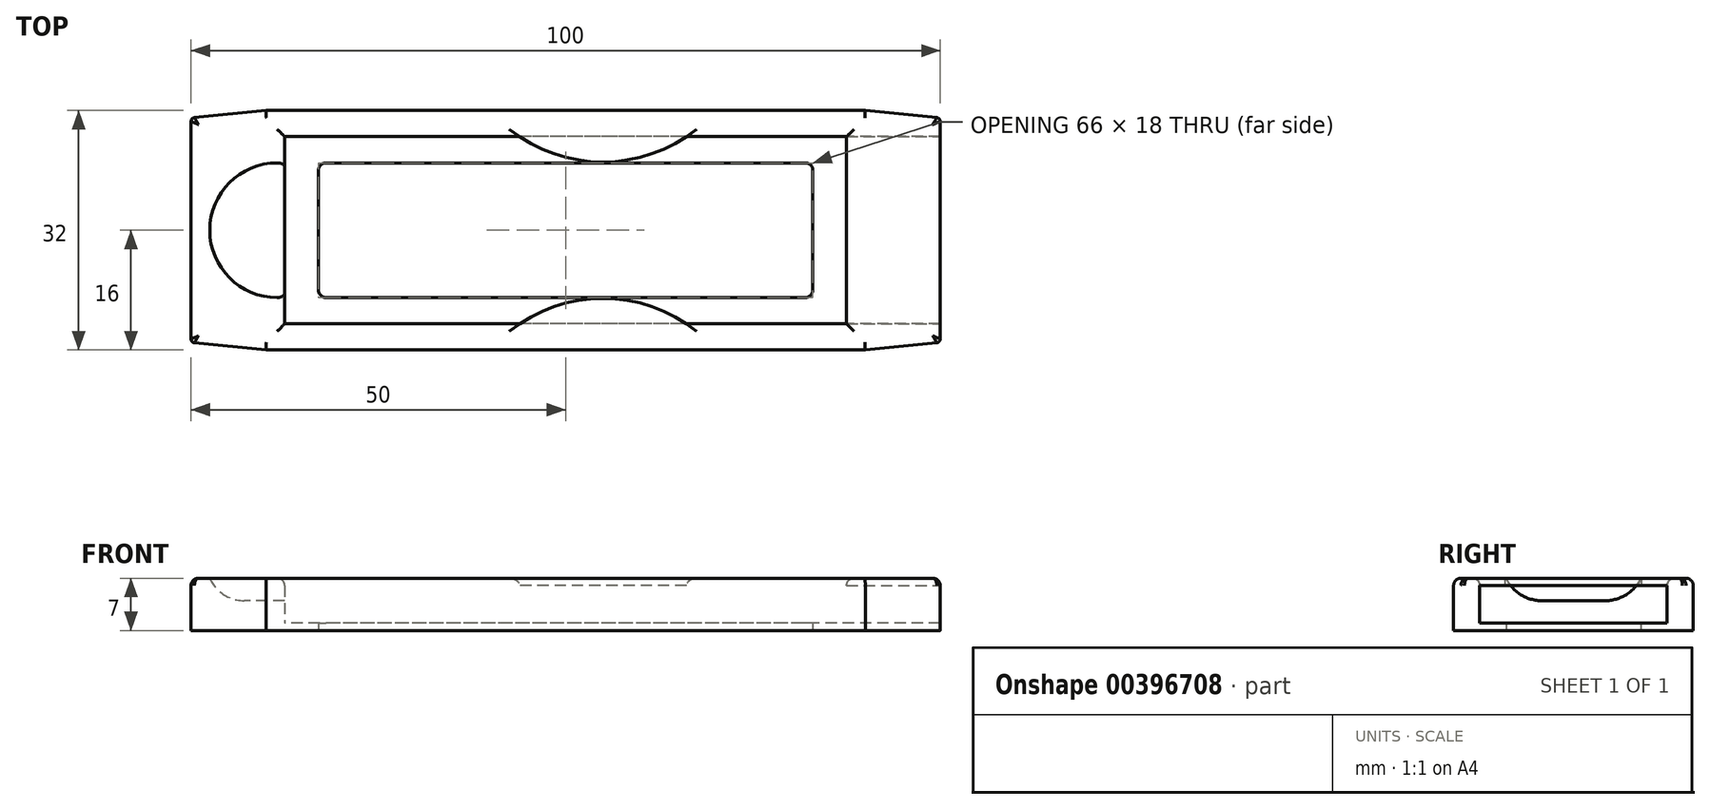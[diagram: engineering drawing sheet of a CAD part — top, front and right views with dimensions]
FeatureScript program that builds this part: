
annotation { "Feature Type Name" : "Feature", "Feature Type Description" : "" }
export const myFeature = defineFeature(function(context is Context, id is Id, definition is map)
    precondition{}
    {
        {
            var Q0;
            Q0=qCreatedBy(makeId("Top.planeOp"),FACE);
            var sketch = newSketch(context, id + "F0", { "sketchPlane" : qUnion([Q0])});
            skLineSegment(sketch, "E0.bottom", {"start": v(37.5, 12.5) * mm, "end": v(-37.5, 12.5) * mm});
            skLineSegment(sketch, "E0.top", {"start": v(37.5, -12.5) * mm, "end": v(-37.5, -12.5) * mm});
            skLineSegment(sketch, "E0.left", {"start": v(37.5, 12.5) * mm, "end": v(37.5, -12.5) * mm});
            skLineSegment(sketch, "E0.right", {"start": v(-37.5, 12.5) * mm, "end": v(-37.5, -12.5) * mm});
            skPoint(sketch, "E0.middle", {"position": v(0, 0) * mm});
            skLineSegment(sketch, "E1.bottom", {"start": v(50, 16) * mm, "end": v(-50, 16) * mm});
            skLineSegment(sketch, "E1.top", {"start": v(50, -16) * mm, "end": v(-50, -16) * mm});
            skLineSegment(sketch, "E1.left", {"start": v(50, 16) * mm, "end": v(50, -16) * mm});
            skLineSegment(sketch, "E1.right", {"start": v(-50, 16) * mm, "end": v(-50, -16) * mm});
            skSolve(sketch);
        }
        {
            var Q0;
            Q0=makeQuery(id+"F0.imprint","IMPRINT",FACE,{"disambiguationData":[TD([[makeQuery(id+"F0.imprint","IMPRINT",EDGE,{"derivedFrom":sQuery(id+"F0.wireOp",EDGE,"E0.bottom")}),-1.0]])]});
            extrude(context, id + "F1", {"entities" : qUnion([Q0]), "depth" : 7 * mm});
        }
        {
            var Q0;
            Q0=makeQuery(id+"F1.opExtrude","SWEPT_EDGE",EDGE,{"disambiguationData":[OSD([sQuery(id+"F0.wireOp",EDGE,"E1.top"),sQuery(id+"F0.wireOp",EDGE,"E1.right")])]});
            var Q1;
            Q1=makeQuery(id+"F1.opExtrude","SWEPT_EDGE",EDGE,{"disambiguationData":[OSD([sQuery(id+"F0.wireOp",EDGE,"E1.top"),sQuery(id+"F0.wireOp",EDGE,"E1.left")])]});
            var Q2;
            Q2=makeQuery(id+"F1.opExtrude","SWEPT_EDGE",EDGE,{"disambiguationData":[OSD([sQuery(id+"F0.wireOp",EDGE,"E1.bottom"),sQuery(id+"F0.wireOp",EDGE,"E1.left")])]});
            var Q3;
            Q3=makeQuery(id+"F1.opExtrude","SWEPT_EDGE",EDGE,{"disambiguationData":[OSD([sQuery(id+"F0.wireOp",EDGE,"E1.bottom"),sQuery(id+"F0.wireOp",EDGE,"E1.right")])]});
            chamfer(context, id + "F2", {"entities" : qUnion([Q0, Q1, Q2, Q3]), "chamferType" : ChamferType.TWO_OFFSETS, "width1" : 10 * mm, "oppositeDirection" : false, "width2" : 1 * mm, "tangentPropagation" : true});
        }
        {
            var Q0;
            {var subQ0=sQuery(id+"F0.wireOp",EDGE,"E1.right");Q0=makeQuery(id+"F2.opChamfer","BLEND_EDGE",EDGE,{"blendedFrom":[makeQuery(id+"F1.opExtrude","SWEPT_EDGE",EDGE,{"disambiguationData":[OSD([sQuery(id+"F0.wireOp",EDGE,"E1.top"),subQ0])]}),makeQuery(id+"F1.opExtrude","SWEPT_FACE",FACE,{"disambiguationData":[OSD([subQ0])]})],"blendedInto":[makeQuery(id+"F1.opExtrude","SWEPT_FACE",FACE,{"disambiguationData":[OSD([subQ0])]})]});}
            var Q1;
            {var subQ0=sQuery(id+"F0.wireOp",EDGE,"E1.left");Q1=makeQuery(id+"F2.opChamfer","BLEND_EDGE",EDGE,{"blendedFrom":[makeQuery(id+"F1.opExtrude","SWEPT_EDGE",EDGE,{"disambiguationData":[OSD([sQuery(id+"F0.wireOp",EDGE,"E1.top"),subQ0])]}),makeQuery(id+"F1.opExtrude","SWEPT_FACE",FACE,{"disambiguationData":[OSD([subQ0])]})],"blendedInto":[makeQuery(id+"F1.opExtrude","SWEPT_FACE",FACE,{"disambiguationData":[OSD([subQ0])]})]});}
            var Q2;
            {var subQ0=sQuery(id+"F0.wireOp",EDGE,"E1.left");Q2=makeQuery(id+"F2.opChamfer","BLEND_EDGE",EDGE,{"blendedFrom":[makeQuery(id+"F1.opExtrude","SWEPT_EDGE",EDGE,{"disambiguationData":[OSD([sQuery(id+"F0.wireOp",EDGE,"E1.bottom"),subQ0])]}),makeQuery(id+"F1.opExtrude","SWEPT_FACE",FACE,{"disambiguationData":[OSD([subQ0])]})],"blendedInto":[makeQuery(id+"F1.opExtrude","SWEPT_FACE",FACE,{"disambiguationData":[OSD([subQ0])]})]});}
            var Q3;
            {var subQ0=sQuery(id+"F0.wireOp",EDGE,"E1.right");Q3=makeQuery(id+"F2.opChamfer","BLEND_EDGE",EDGE,{"blendedFrom":[makeQuery(id+"F1.opExtrude","SWEPT_EDGE",EDGE,{"disambiguationData":[OSD([sQuery(id+"F0.wireOp",EDGE,"E1.bottom"),subQ0])]}),makeQuery(id+"F1.opExtrude","SWEPT_FACE",FACE,{"disambiguationData":[OSD([subQ0])]})],"blendedInto":[makeQuery(id+"F1.opExtrude","SWEPT_FACE",FACE,{"disambiguationData":[OSD([subQ0])]})]});}
            fillet(context, id + "F3", {"entities" : qUnion([Q0, Q1, Q2, Q3]), "radius" : .5 * mm, "tangentPropagation" : true, "allowEdgeOverflow" : false});
        }
        {
            var Q0;
            Q0=qCreatedBy(makeId("Top.planeOp"),FACE);
            var sketch = newSketch(context, id + "F4", { "sketchPlane" : qUnion([Q0])});
            skLineSegment(sketch, "E2.bottom", {"start": v(38, 13) * mm, "end": v(-38, 13) * mm});
            skLineSegment(sketch, "E2.top", {"start": v(38, -13) * mm, "end": v(-38, -13) * mm});
            skLineSegment(sketch, "E2.left", {"start": v(38, 13) * mm, "end": v(38, -13) * mm});
            skLineSegment(sketch, "E2.right", {"start": v(-38, 13) * mm, "end": v(-38, -13) * mm});
            skPoint(sketch, "E2.middle", {"position": v(0, 0) * mm});
            skLineSegment(sketch, "E3.bottom", {"start": v(33, 9) * mm, "end": v(-33, 9) * mm});
            skLineSegment(sketch, "E3.top", {"start": v(33, -9) * mm, "end": v(-33, -9) * mm});
            skLineSegment(sketch, "E3.left", {"start": v(33, 9) * mm, "end": v(33, -9) * mm});
            skLineSegment(sketch, "E3.right", {"start": v(-33, 9) * mm, "end": v(-33, -9) * mm});
            skSolve(sketch);
        }
        {
            var Q0;
            Q0 = qSketchRegion(id + "F4", true);
            extrude(context, id + "F5", {"entities" : qUnion([Q0]), "operationType" : NewBodyOperationType.ADD, "depth" : 1 * mm});
        }
        {
            var Q0;
            Q0=makeQuery(id+"F5.opExtrude","SWEPT_EDGE",EDGE,{"disambiguationData":[OSD([sQuery(id+"F4.wireOp",EDGE,"E3.bottom"),sQuery(id+"F4.wireOp",EDGE,"E3.right")])]});
            var Q1;
            Q1=makeQuery(id+"F5.opExtrude","SWEPT_EDGE",EDGE,{"disambiguationData":[OSD([sQuery(id+"F4.wireOp",EDGE,"E3.bottom"),sQuery(id+"F4.wireOp",EDGE,"E3.left")])]});
            var Q2;
            Q2=makeQuery(id+"F5.opExtrude","SWEPT_EDGE",EDGE,{"disambiguationData":[OSD([sQuery(id+"F4.wireOp",EDGE,"E3.top"),sQuery(id+"F4.wireOp",EDGE,"E3.left")])]});
            var Q3;
            Q3=makeQuery(id+"F5.opExtrude","SWEPT_EDGE",EDGE,{"disambiguationData":[OSD([sQuery(id+"F4.wireOp",EDGE,"E3.top"),sQuery(id+"F4.wireOp",EDGE,"E3.right")])]});
            fillet(context, id + "F6", {"entities" : qUnion([Q0, Q1, Q2, Q3]), "radius" : 1 * mm, "tangentPropagation" : true, "allowEdgeOverflow" : false});
        }
        {
            var Q0;
            Q0=makeQuery(id+"F1.opExtrude","CAP_EDGE",EDGE,{"disambiguationData":[OSD([sQuery(id+"F0.wireOp",EDGE,"E1.bottom")])],"isStart":false});
            var Q1;
            Q1=makeQuery(id+"F1.opExtrude","CAP_EDGE",EDGE,{"disambiguationData":[OSD([sQuery(id+"F0.wireOp",EDGE,"E1.top")])],"isStart":false});
            var Q2;
            Q2=makeQuery(id+"F1.opExtrude","CAP_EDGE",EDGE,{"disambiguationData":[OSD([sQuery(id+"F0.wireOp",EDGE,"E1.right")])],"isStart":false});
            var Q3;
            Q3=makeQuery(id+"F1.opExtrude","CAP_EDGE",EDGE,{"disambiguationData":[OSD([sQuery(id+"F0.wireOp",EDGE,"E1.left")])],"isStart":false});
            var Q4;
            Q4=makeQuery(id+"F1.opExtrude","CAP_EDGE",EDGE,{"disambiguationData":[OSD([sQuery(id+"F0.wireOp",EDGE,"E0.left")])],"isStart":false});
            var Q5;
            Q5=makeQuery(id+"F1.opExtrude","CAP_EDGE",EDGE,{"disambiguationData":[OSD([sQuery(id+"F0.wireOp",EDGE,"E0.top")])],"isStart":false});
            var Q6;
            Q6=makeQuery(id+"F1.opExtrude","CAP_EDGE",EDGE,{"disambiguationData":[OSD([sQuery(id+"F0.wireOp",EDGE,"E0.right")])],"isStart":false});
            var Q7;
            Q7=makeQuery(id+"F1.opExtrude","CAP_EDGE",EDGE,{"disambiguationData":[OSD([sQuery(id+"F0.wireOp",EDGE,"E0.bottom")])],"isStart":false});
            fillet(context, id + "F7", {"entities" : qUnion([Q0, Q1, Q2, Q3, Q4, Q5, Q6, Q7]), "radius" : 1 * mm, "tangentPropagation" : true, "allowEdgeOverflow" : false});
        }
        {
            var Q0;
            Q0=makeQuery(id+"F1.opExtrude","SWEPT_FACE",FACE,{"disambiguationData":[OSD([sQuery(id+"F0.wireOp",EDGE,"E1.left")])]});
            var sketch = newSketch(context, id + "F8", { "sketchPlane" : qUnion([Q0])});
            skLineSegment(sketch, "E4.bottom", {"start": v(12.5, 6) * mm, "end": v(-12.5, 6) * mm});
            skLineSegment(sketch, "E4.top", {"start": v(12.5, 1) * mm, "end": v(-12.5, 1) * mm});
            skLineSegment(sketch, "E4.left", {"start": v(12.5, 6) * mm, "end": v(12.5, 1) * mm});
            skLineSegment(sketch, "E4.right", {"start": v(-12.5, 6) * mm, "end": v(-12.5, 1) * mm});
            skPoint(sketch, "E4.middle", {"position": v(0, 3.5) * mm});
            skPoint(sketch, "E4.middle.positionSnap0", {"position": v(0, 0) * mm});
            skPoint(sketch, "E4.centerSnap0", {"position": v(0, 0) * mm});
            skSolve(sketch);
        }
        {
            var Q0;
            Q0=makeQuery(id+"F8.imprint","IMPRINT",FACE,{"disambiguationData":[TD([[makeQuery(id+"F8.imprint","IMPRINT",EDGE,{"derivedFrom":sQuery(id+"F8.wireOp",EDGE,"E4.bottom")}),1.0]])]});
            extrude(context, id + "F9", {"entities" : qUnion([Q0]), "operationType" : NewBodyOperationType.REMOVE, "oppositeDirection" : true, "depth" : 15 * mm});
        }
        {
            var Q0;
            Q0=makeQuery(id+"F1.opExtrude","CAP_FACE",FACE,{"disambiguationData":[OSD([sQuery(id+"F0.wireOp",EDGE,"E0.bottom"),sQuery(id+"F0.wireOp",EDGE,"E0.top"),sQuery(id+"F0.wireOp",EDGE,"E0.left"),sQuery(id+"F0.wireOp",EDGE,"E0.right"),sQuery(id+"F0.wireOp",EDGE,"E1.bottom"),sQuery(id+"F0.wireOp",EDGE,"E1.top"),sQuery(id+"F0.wireOp",EDGE,"E1.left"),sQuery(id+"F0.wireOp",EDGE,"E1.right")])],"isStart":false});
            var sketch = newSketch(context, id + "F10", { "sketchPlane" : qUnion([Q0])});
            skCircle(sketch, "E5", {"center": v(-38.5, 0) * mm, "radius": 9 * mm});
            skSolve(sketch);
        }
        {
            var Q0;
            Q0 = qSketchRegion(id + "F10", true);
            extrude(context, id + "F11", {"entities" : qUnion([Q0]), "operationType" : NewBodyOperationType.REMOVE, "oppositeDirection" : true, "depth" : 3 * mm});
        }
        {
            var Q0;
            Q0=makeQuery(id+"F11.boolean.opBoolean","COPY",EDGE,{"derivedFrom":makeQuery(id+"F11.opExtrude","CAP_EDGE",EDGE,{"disambiguationData":[OSD([sQuery(id+"F10.wireOp",EDGE,"E5")])],"isStart":false})});
            fillet(context, id + "F12", {"entities" : qUnion([Q0]), "radius" : 5 * mm, "tangentPropagation" : true, "allowEdgeOverflow" : false});
        }
        {
            var Q0;
            Q0=makeQuery(id+"F1.opExtrude","CAP_FACE",FACE,{"disambiguationData":[OSD([sQuery(id+"F0.wireOp",EDGE,"E0.bottom"),sQuery(id+"F0.wireOp",EDGE,"E0.top"),sQuery(id+"F0.wireOp",EDGE,"E0.left"),sQuery(id+"F0.wireOp",EDGE,"E0.right"),sQuery(id+"F0.wireOp",EDGE,"E1.bottom"),sQuery(id+"F0.wireOp",EDGE,"E1.top"),sQuery(id+"F0.wireOp",EDGE,"E1.left"),sQuery(id+"F0.wireOp",EDGE,"E1.right")])],"isStart":false});
            var sketch = newSketch(context, id + "F13", { "sketchPlane" : qUnion([Q0])});
            skArc(sketch, "E6", {"start": v(17.5, -13.5) * mm, "mid": v(5, -9.11) * mm, "end": v(-7.5, -13.5) * mm});
            skLineSegment(sketch, "E7", {"start": v(17.5, -13.5) * mm, "end": v(-7.5, -13.5) * mm});
            skSolve(sketch);
        }
        {
            var Q0;
            Q0 = qSketchRegion(id + "F13", true);
            extrude(context, id + "F14", {"entities" : qUnion([Q0]), "operationType" : NewBodyOperationType.ADD, "oppositeDirection" : true, "depth" : 1 * mm});
        }
        {
            var Q0;
            Q0=makeQuery(id+"F14.boolean.opBoolean","MERGE",FACE,{"derivedFrom":[makeQuery(id+"F1.opExtrude","CAP_FACE",FACE,{"disambiguationData":[OSD([sQuery(id+"F0.wireOp",EDGE,"E0.bottom"),sQuery(id+"F0.wireOp",EDGE,"E0.top"),sQuery(id+"F0.wireOp",EDGE,"E0.left"),sQuery(id+"F0.wireOp",EDGE,"E0.right"),sQuery(id+"F0.wireOp",EDGE,"E1.bottom"),sQuery(id+"F0.wireOp",EDGE,"E1.top"),sQuery(id+"F0.wireOp",EDGE,"E1.left"),sQuery(id+"F0.wireOp",EDGE,"E1.right")])],"isStart":false}),makeQuery(id+"F14.opExtrude","CAP_FACE",FACE,{"disambiguationData":[OSD([sQuery(id+"F13.wireOp",EDGE,"E6"),sQuery(id+"F13.wireOp",EDGE,"E7")])],"isStart":true})]});
            var sketch = newSketch(context, id + "F15", { "sketchPlane" : qUnion([Q0])});
            skArc(sketch, "E8", {"start": v(-7.5, 13.5) * mm, "mid": v(5, 9.11) * mm, "end": v(17.5, 13.5) * mm});
            skLineSegment(sketch, "E9", {"start": v(17.5, 13.5) * mm, "end": v(-7.5, 13.5) * mm});
            skSolve(sketch);
        }
        {
            var Q0;
            Q0 = qSketchRegion(id + "F15", true);
            extrude(context, id + "F16", {"entities" : qUnion([Q0]), "operationType" : NewBodyOperationType.ADD, "oppositeDirection" : true, "depth" : 1 * mm});
        }
    });
